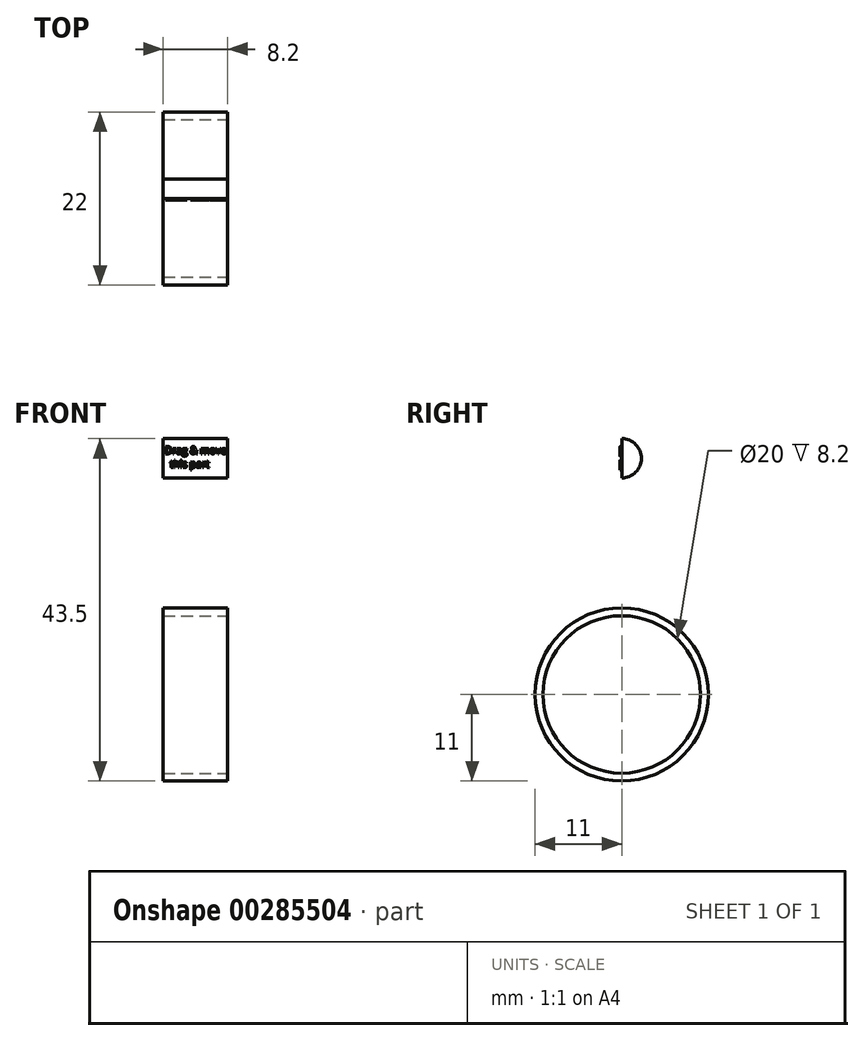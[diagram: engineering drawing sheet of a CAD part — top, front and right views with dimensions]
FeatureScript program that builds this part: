
annotation { "Feature Type Name" : "Feature", "Feature Type Description" : "" }
export const myFeature = defineFeature(function(context is Context, id is Id, definition is map)
    precondition{}
    {
        {
            var Q0;
            Q0=qCreatedBy(makeId("Right.planeOp"),FACE);
            var sketch = newSketch(context, id + "F0", { "sketchPlane" : qUnion([Q0])});
            skCircle(sketch, "E0", {"center": v(0, 0) * mm, "radius": 10 * mm});
            skCircle(sketch, "E1", {"center": v(0, 0) * mm, "radius": 11 * mm});
            skArc(sketch, "E2", {"start": v(0, 27.5) * mm, "mid": v(2.5, 30) * mm, "end": v(0, 32.5) * mm});
            skLineSegment(sketch, "E3", {"start": v(0, 32.5) * mm, "end": v(0, 27.5) * mm});
            skSolve(sketch);
        }
        {
            var Q0;
            Q0=qSketchRegion(id+"F0",true);
            extrude(context, id + "F1", {"entities" : qUnion([Q0]), "oppositeDirection" : true, "depth" : 8.2 * mm});
        }
        {
            var Q0;
            Q0=makeQuery(id+"F1.opExtrude","SWEPT_FACE",FACE,{"disambiguationData":[OSD([sQuery(id+"F0.wireOp",EDGE,"E3")])]});
            var sketch = newSketch(context, id + "F2", { "sketchPlane" : qUnion([Q0])});
            skText(sketch, "E4", { "text": "Drag & move\n  this part", "fontName": "OpenSans-Regular.ttf"});
            const initialGuessF2  = {"E4": [-0.008, 0.03057, 1, 0, 0.00093]};
            skSetInitialGuess(sketch, initialGuessF2);
            skSolve(sketch);
        }
        {
            var Q0;
            Q0=qSketchRegion(id+"F2",true);
            extrude(context, id + "F3", {"entities" : qUnion([Q0]), "operationType" : NewBodyOperationType.ADD, "depth" : 0.2 * mm});
        }
    });
